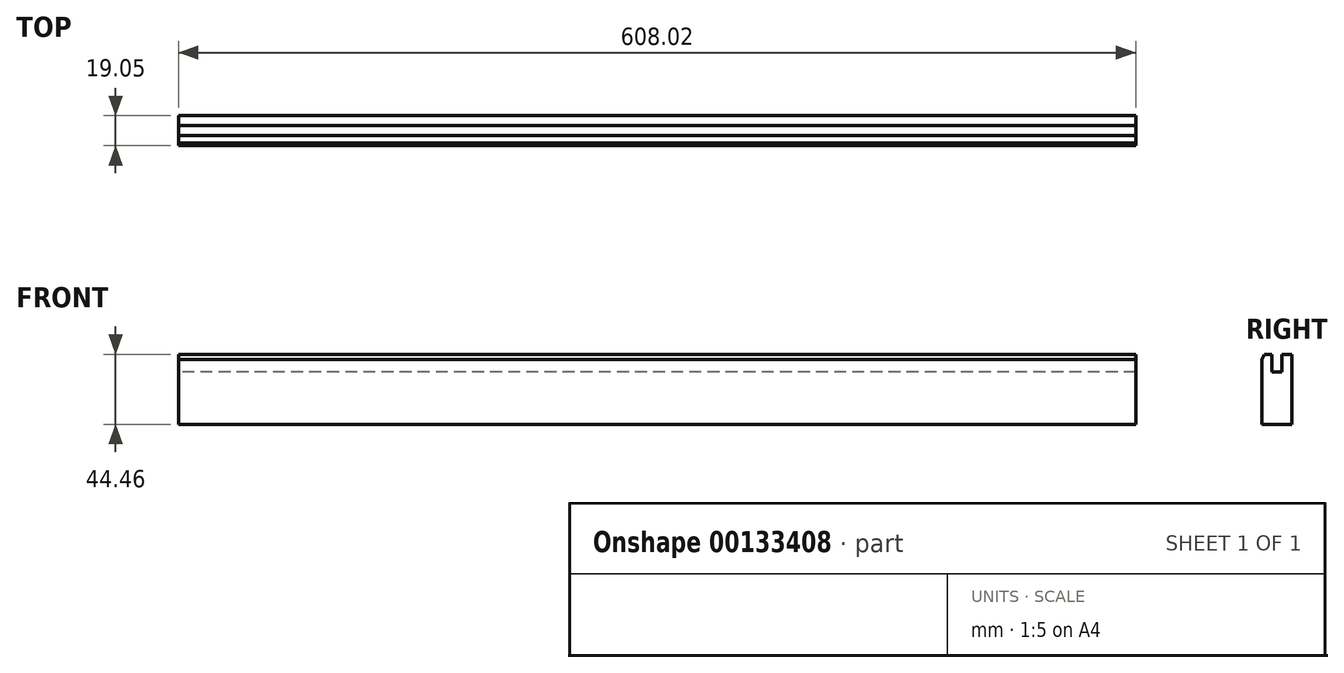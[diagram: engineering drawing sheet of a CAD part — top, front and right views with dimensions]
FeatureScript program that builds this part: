
annotation { "Feature Type Name" : "Feature", "Feature Type Description" : "" }
export const myFeature = defineFeature(function(context is Context, id is Id, definition is map)
    precondition{}
    {
        {
            var Q0;
            Q0=qCreatedBy(makeId("Front.planeOp"),FACE);
            var sketch = newSketch(context, id + "F0", { "sketchPlane" : qUnion([Q0])});
            skLineSegment(sketch, "E0.bottom", {"start": v(-304, 22.22) * mm, "end": v(304, 22.22) * mm});
            skLineSegment(sketch, "E0.top", {"start": v(-304, -22.22) * mm, "end": v(304, -22.22) * mm});
            skLineSegment(sketch, "E0.left", {"start": v(-304, 22.22) * mm, "end": v(-304, -22.22) * mm});
            skLineSegment(sketch, "E0.right", {"start": v(304, 22.22) * mm, "end": v(304, -22.22) * mm});
            skPoint(sketch, "E0.middle", {"position": v(0, 0) * mm});
            skSolve(sketch);
        }
        {
            var Q0;
            Q0 = qSketchRegion(id + "F0", true);
            extrude(context, id + "F1", {"entities" : qUnion([Q0]), "depth" : 19.05 * mm});
        }
        {
            var Q0;
            Q0=makeQuery(id+"F1.opExtrude","SWEPT_FACE",FACE,{"disambiguationData":[OSD([sQuery(id+"F0.wireOp",EDGE,"E0.left")])]});
            var sketch = newSketch(context, id + "F2", { "sketchPlane" : qUnion([Q0])});
            skLineSegment(sketch, "E1", {"start": v(9.53, 22.22) * mm, "end": v(9.53, -22.23) * mm, "construction": true});
            skLineSegment(sketch, "E2.bottom", {"start": v(6.35, 22.22) * mm, "end": v(12.7, 22.22) * mm});
            skLineSegment(sketch, "E2.top", {"start": v(6.35, 11.11) * mm, "end": v(12.7, 11.11) * mm});
            skLineSegment(sketch, "E2.left", {"start": v(6.35, 22.22) * mm, "end": v(6.35, 11.11) * mm});
            skLineSegment(sketch, "E2.right", {"start": v(12.7, 22.22) * mm, "end": v(12.7, 11.11) * mm});
            skSolve(sketch);
        }
        {
            var Q0;
            Q0 = qSketchRegion(id + "F2", true);
            extrude(context, id + "F3", {"entities" : qUnion([Q0]), "operationType" : NewBodyOperationType.REMOVE, "endBound" : BoundingType.THROUGH_ALL, "oppositeDirection" : true, "depth" : 25.4 * mm});
        }
        {
            var Q0;
            Q0=makeQuery(id+"F1.opExtrude","CAP_EDGE",EDGE,{"disambiguationData":[OSD([sQuery(id+"F0.wireOp",EDGE,"E0.bottom")])],"isStart":false});
            chamfer(context, id + "F4", {"entities" : qUnion([Q0]), "chamferType" : ChamferType.TWO_OFFSETS, "width1" : 1.59 * mm, "oppositeDirection" : false, "width2" : 3.17 * mm, "tangentPropagation" : true});
        }
    });
